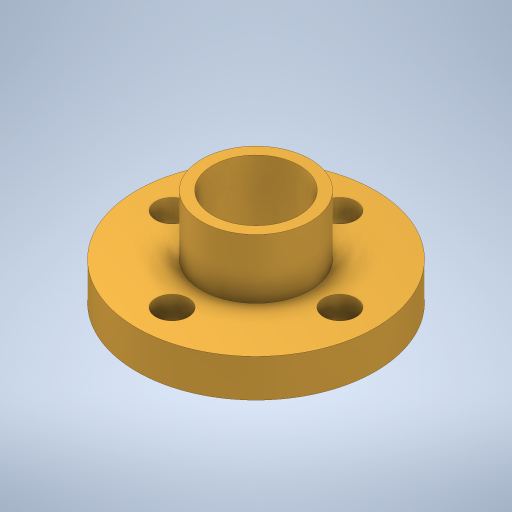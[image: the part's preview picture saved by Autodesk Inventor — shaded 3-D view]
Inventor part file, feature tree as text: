
AUTODESK INVENTOR PART (.ipt)
format: ipt  version: 2023.1 (Build 271208000, 208)  size: 277,504 bytes
history: native  units: mm
features: extrude x2, other x1, sketch x1, hole x1, pattern_circular x1
ambient origin geometry x8: Origin, YZ Plane, XZ Plane, XY Plane, X Axis, Y Axis, Z Axis, Center Point
bodies: Body1 (feature_tree)
feature tree (6):
  other  "Brass Nut"
  sketch  "Sketch1"  dims[d1=22.0mm d2=15.5mm d4=10.0mm d5=3.5mm d6=0.0mm d7=3.0mm d8=6.0mm d9=4.0mm d10=2.0mm d11=90.0deg d12=8.0mm d13=20.594885mm d14=40.0mm d15=360.0deg d17=8.0mm d18=9.0mm d19=1.5mm d20=0.0mm d21=0.0mm]
  extrude  "Extrusion1"  Depth=1.5mm
  hole  "Hole1"  [1 undecoded]
  pattern_circular  "Circular Pattern1"  [2 undecoded]
  extrude  "Extrusion2"  Depth=1.5mm TaperAngle=360.0deg
note: 3 required parameter values undecoded (feature->parameter linkage not recoverable at this tier; creation-order binding heuristic only, values carry confidence <= 0.55)
